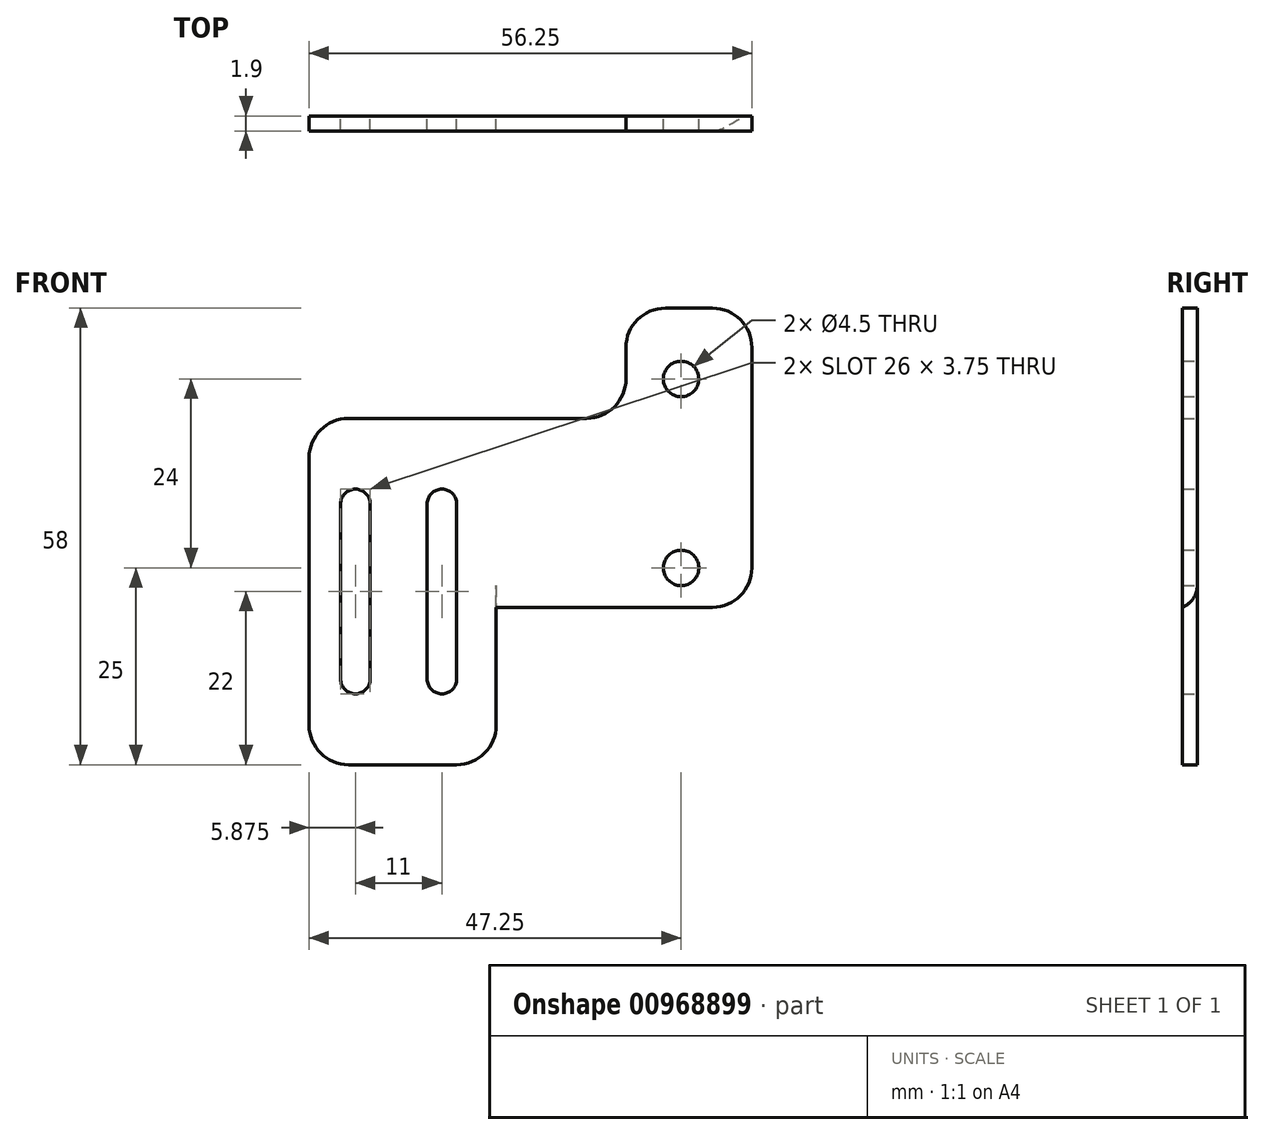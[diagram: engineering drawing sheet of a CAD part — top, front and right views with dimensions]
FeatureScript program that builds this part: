
annotation { "Feature Type Name" : "Feature", "Feature Type Description" : "" }
export const myFeature = defineFeature(function(context is Context, id is Id, definition is map)
    precondition{}
    {
        {
            var Q0;
            Q0=qCreatedBy(makeId("Front.planeOp"),FACE);
            var sketch = newSketch(context, id + "F0", { "sketchPlane" : qUnion([Q0])});
            skLineSegment(sketch, "E0.left", {"start": v(0, -5) * mm, "end": v(0, -33) * mm});
            skCircle(sketch, "E1", {"center": v(-9, -9) * mm, "radius": 2.25 * mm});
            skCircle(sketch, "E2", {"center": v(-9, -33) * mm, "radius": 2.25 * mm});
            skLineSegment(sketch, "E3.left", {"start": v(-16, -5) * mm, "end": v(-16, -9) * mm});
            skLineSegment(sketch, "E4.top", {"start": v(-51.25, -58) * mm, "end": v(-37.5, -58) * mm});
            skLineSegment(sketch, "E4.right", {"start": v(-32.5, -43) * mm, "end": v(-32.5, -53) * mm});
            skLineSegment(sketch, "E5.bottom", {"start": v(-39.37, -23) * mm, "end": v(-39.38, -23) * mm});
            skLineSegment(sketch, "E5.top", {"start": v(-39.37, -49) * mm, "end": v(-39.38, -49) * mm});
            skLineSegment(sketch, "E5.left", {"start": v(-41.25, -24.88) * mm, "end": v(-41.25, -47.13) * mm});
            skLineSegment(sketch, "E5.right", {"start": v(-37.5, -24.88) * mm, "end": v(-37.5, -47.13) * mm});
            skLineSegment(sketch, "E6.bottom", {"start": v(-50.38, -23) * mm, "end": v(-50.38, -23) * mm});
            skLineSegment(sketch, "E6.top", {"start": v(-50.38, -49) * mm, "end": v(-50.38, -49) * mm});
            skLineSegment(sketch, "E6.left", {"start": v(-52.25, -24.88) * mm, "end": v(-52.25, -47.13) * mm});
            skLineSegment(sketch, "E6.right", {"start": v(-48.5, -24.88) * mm, "end": v(-48.5, -47.13) * mm});
            skLineSegment(sketch, "E7", {"start": v(-5, 0) * mm, "end": v(-11, 0) * mm});
            skLineSegment(sketch, "E8", {"start": v(-27.5, -38) * mm, "end": v(-5, -38) * mm});
            skLineSegment(sketch, "E9", {"start": v(-21, -14) * mm, "end": v(-51.25, -14) * mm});
            skLineSegment(sketch, "E10", {"start": v(-56.25, -53) * mm, "end": v(-56.25, -19) * mm});
            skPoint(sketch, "E11.visualSharp", {"position": v(-56.25, -14) * mm});
            skArc(sketch, "E11.filletArc", {"start": v(-51.25, -14) * mm, "mid": v(-54.79, -15.46) * mm, "end": v(-56.25, -19) * mm});
            skPoint(sketch, "E12.visualSharp", {"position": v(-56.25, -58) * mm});
            skArc(sketch, "E12.filletArc", {"start": v(-56.25, -53) * mm, "mid": v(-54.79, -56.54) * mm, "end": v(-51.25, -58) * mm});
            skPoint(sketch, "E13.visualSharp", {"position": v(-32.5, -58) * mm});
            skArc(sketch, "E13.filletArc", {"start": v(-37.5, -58) * mm, "mid": v(-33.96, -56.54) * mm, "end": v(-32.5, -53) * mm});
            skPoint(sketch, "E14.visualSharp", {"position": v(-32.5, -38) * mm});
            skPoint(sketch, "E15.visualSharp", {"position": v(0, -38) * mm});
            skArc(sketch, "E15.filletArc", {"start": v(-5, -38) * mm, "mid": v(-1.46, -36.54) * mm, "end": v(0, -33) * mm});
            skPoint(sketch, "E16.visualSharp", {"position": v(0, 0) * mm});
            skArc(sketch, "E16.filletArc", {"start": v(0, -5) * mm, "mid": v(-1.46, -1.46) * mm, "end": v(-5, 0) * mm});
            skPoint(sketch, "E17.visualSharp", {"position": v(-16, 0) * mm});
            skArc(sketch, "E17.filletArc", {"start": v(-11, 0) * mm, "mid": v(-14.54, -1.46) * mm, "end": v(-16, -5) * mm});
            skPoint(sketch, "E18.visualSharp", {"position": v(-16, -14) * mm});
            skArc(sketch, "E18.filletArc", {"start": v(-21, -14) * mm, "mid": v(-17.46, -12.54) * mm, "end": v(-16, -9) * mm});
            skPoint(sketch, "E19.visualSharp", {"position": v(-52.25, -23) * mm});
            skArc(sketch, "E19.filletArc", {"start": v(-50.38, -23) * mm, "mid": v(-51.7, -23.55) * mm, "end": v(-52.25, -24.88) * mm});
            skPoint(sketch, "E20.visualSharp", {"position": v(-48.5, -23) * mm});
            skArc(sketch, "E20.filletArc", {"start": v(-48.5, -24.88) * mm, "mid": v(-49.05, -23.55) * mm, "end": v(-50.38, -23) * mm});
            skPoint(sketch, "E21.visualSharp", {"position": v(-52.25, -49) * mm});
            skArc(sketch, "E21.filletArc", {"start": v(-52.25, -47.13) * mm, "mid": v(-51.7, -48.45) * mm, "end": v(-50.38, -49) * mm});
            skPoint(sketch, "E22.visualSharp", {"position": v(-48.5, -49) * mm});
            skArc(sketch, "E22.filletArc", {"start": v(-50.38, -49) * mm, "mid": v(-49.05, -48.45) * mm, "end": v(-48.5, -47.13) * mm});
            skPoint(sketch, "E23.visualSharp", {"position": v(-41.25, -49) * mm});
            skArc(sketch, "E23.filletArc", {"start": v(-41.25, -47.13) * mm, "mid": v(-40.7, -48.45) * mm, "end": v(-39.37, -49) * mm});
            skPoint(sketch, "E24.visualSharp", {"position": v(-37.5, -49) * mm});
            skArc(sketch, "E24.filletArc", {"start": v(-39.38, -49) * mm, "mid": v(-38.05, -48.45) * mm, "end": v(-37.5, -47.13) * mm});
            skPoint(sketch, "E25.visualSharp", {"position": v(-37.5, -23) * mm});
            skArc(sketch, "E25.filletArc", {"start": v(-37.5, -24.88) * mm, "mid": v(-38.05, -23.55) * mm, "end": v(-39.38, -23) * mm});
            skPoint(sketch, "E26.visualSharp", {"position": v(-41.25, -23) * mm});
            skArc(sketch, "E26.filletArc", {"start": v(-39.37, -23) * mm, "mid": v(-40.7, -23.55) * mm, "end": v(-41.25, -24.88) * mm});
            skLineSegment(sketch, "E27", {"start": v(-27.5, -38) * mm, "end": v(-32.5, -38) * mm});
            skLineSegment(sketch, "E28", {"start": v(-32.5, -43) * mm, "end": v(-32.5, -38) * mm});
            skSolve(sketch);
        }
        {
            var Q0;
            Q0=makeQuery(id+"F0.imprint","IMPRINT",FACE,{"disambiguationData":[TD([[makeQuery(id+"F0.imprint","IMPRINT",EDGE,{"derivedFrom":sQuery(id+"F0.wireOp",EDGE,"E0.left")}),-1.0]])]});
            extrude(context, id + "F1", {"entities" : qUnion([Q0]), "depth" : 1.9 * mm, "offsetDistance" : 25 * mm});
        }
        {
            var Q0;
            Q0=makeQuery(id+"F1.opExtrude","CAP_EDGE",EDGE,{"disambiguationData":[OSD([sQuery(id+"F0.wireOp",EDGE,"E8"),sQuery(id+"F0.wireOp",EDGE,"E27")])],"isStart":true});
            fillet(context, id + "F2", {"entities" : qUnion([Q0]), "radius" : 3 * mm, "allowEdgeOverflow" : false});
        }
    });
